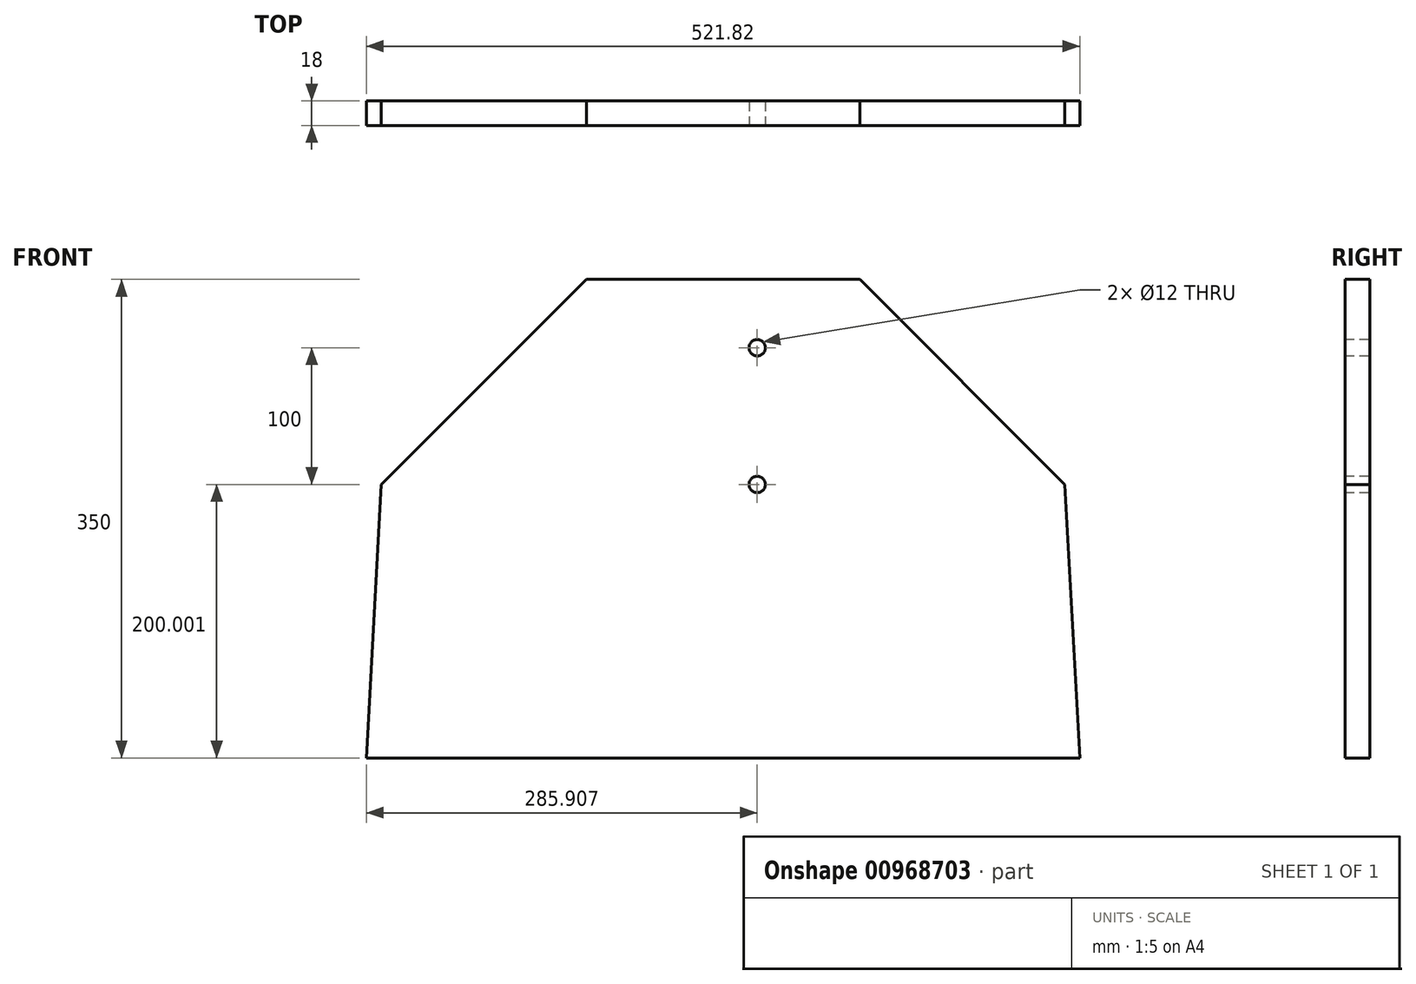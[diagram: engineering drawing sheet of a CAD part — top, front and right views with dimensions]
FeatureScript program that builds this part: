
annotation { "Feature Type Name" : "Feature", "Feature Type Description" : "" }
export const myFeature = defineFeature(function(context is Context, id is Id, definition is map)
    precondition{}
    {
        {
            var Q0;
            Q0=qCreatedBy(makeId("Front.planeOp"),FACE);
            var sketch = newSketch(context, id + "F0", { "sketchPlane" : qUnion([Q0])});
            skLineSegment(sketch, "E0.bottom", {"start": v(180.36, -66.98) * mm, "end": v(441.27, -66.98) * mm});
            skLineSegment(sketch, "E0.top", {"start": v(180.36, 283.02) * mm, "end": v(280.36, 283.02) * mm});
            skLineSegment(sketch, "E0.right", {"start": v(441.27, -66.98) * mm, "end": v(430.36, 133.02) * mm});
            skLineSegment(sketch, "E1", {"start": v(280.36, 283.02) * mm, "end": v(430.36, 133.02) * mm});
            skLineSegment(sketch, "E2", {"start": v(180.36, 283.02) * mm, "end": v(180.36, -66.98) * mm});
            skSolve(sketch);
        }
        {
            var Q0;
            Q0 = qSketchRegion(id + "F0", true);
            extrude(context, id + "F1", {"entities" : qUnion([Q0]), "depth" : 18 * mm, "offsetDistance" : 25.4 * mm});
        }
        {
            var Q0;
            Q0=makeQuery(id+"F1.opExtrude","SWEPT_BODY",BODY,{"disambiguationData":[OSD([sQuery(id+"F0.wireOp",EDGE,"E0.bottom"),sQuery(id+"F0.wireOp",EDGE,"E0.top"),sQuery(id+"F0.wireOp",EDGE,"E0.right"),sQuery(id+"F0.wireOp",EDGE,"E1"),sQuery(id+"F0.wireOp",EDGE,"E2")])]});
            var Q1;
            Q1=makeQuery(id+"F1.opExtrude","SWEPT_FACE",FACE,{"disambiguationData":[OSD([sQuery(id+"F0.wireOp",EDGE,"E2")])]});
            mirror(context, id + "F2", {"operationType" : NewBodyOperationType.ADD, "entities" : qUnion([Q0]), "mirrorPlane" : qUnion([Q1])});
        }
        {
            var Q0;
            {var subQ0=makeQuery(id+"F1.opExtrude","CAP_FACE",FACE,{"disambiguationData":[OSD([sQuery(id+"F0.wireOp",EDGE,"E0.bottom"),sQuery(id+"F0.wireOp",EDGE,"E0.top"),sQuery(id+"F0.wireOp",EDGE,"E0.right"),sQuery(id+"F0.wireOp",EDGE,"E1"),sQuery(id+"F0.wireOp",EDGE,"E2")])],"isStart":false});Q0=makeQuery(id+"F2.boolean.opBoolean","MERGE",FACE,{"derivedFrom":[subQ0,makeQuery(id+"F2.opPattern","COPY",FACE,{"derivedFrom":subQ0,"instanceName":"1"})]});}
            var sketch = newSketch(context, id + "F3", { "sketchPlane" : qUnion([Q0])});
            skCircle(sketch, "E3", {"center": v(205.36, 233.02) * mm, "radius": 6 * mm});
            skCircle(sketch, "E4", {"center": v(205.36, 133.02) * mm, "radius": 6 * mm});
            skSolve(sketch);
        }
        {
            var Q0;
            Q0 = qSketchRegion(id + "F3", true);
            extrude(context, id + "F4", {"entities" : qUnion([Q0]), "operationType" : NewBodyOperationType.REMOVE, "oppositeDirection" : true, "depth" : 25 * mm, "offsetDistance" : 25 * mm});
        }
    });
